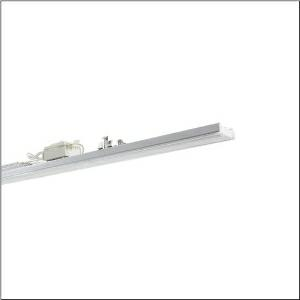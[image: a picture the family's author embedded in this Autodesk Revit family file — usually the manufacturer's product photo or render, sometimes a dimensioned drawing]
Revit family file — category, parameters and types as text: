
# Revit family: licross_r__11_recessed_mo_51tl10dn495g_bfc4
name_source: partatom
category: Lighting Fixtures
units: mm (PartAtom-declared; Revit-internal decimal feet)

## family parameters
Cut with Voids When Loaded = No
Host = Face
Light Source = No
Part Type = Normal
Room Calculation Point = No
Round Connector Dimension = Use Diameter
Shared = No

## types (1)
- --- (1 x LED, 9960 lm, 56.7 W, 4000K)
    Apparent Load = 57 VA
    CIE Flux Codes = 50 81 96 100 100
    Color Rendering = 80
    Color Temperature = 4000K
    Default Elevation = 1800 mm
    Description = Licross® 11 Recessed MO, luminaire insert, of sheet steel, coil coated, white, length: 1.500mm, width: 66mm, height: 67mm, LED rated luminous flux: 9.960lm, light colour: 840, control gear: DALI 2, with plug, 5-pole, with phase selection, mains connection: 220..240V, AC, 50/60Hz, rated input power: 57W, halogen-free wiring, primary optical cover: cover, of PMMA, light emission: direct distribution, primary light characteristic: symmetric, protection rating (complete): IP40, insulation class (complete): insulation class I (protective earthing), certification: CE, ENEC, VDE, UKCA, protection symbol: D if used in an environment without relevant dust loads with corresponding accessories, impact resistance: IK06, permissible ambient temperature for indoor applications: -25..+35°C, corresponds to IFS (International Featured Standards) requirements for safety and quality in the food industry, reducing of maximum allowable ambient temperature of 5°C with ceiling mounting, LABS conformity tested according to VDMA 24364:2018-05, packaging unit: 1 piece
    Height = 58 mm
    Lamp = 1 x LED
    Lamp Light Flux = 9960 lm
    Lamp Power = 56.7 W
    Lamp count = 1
    Length = 1500 mm
    Luminous efficacy = 176 lm/W
    Manufacturer = Siteco
    ModVariant = No
    Model = 51TL10DN495G
    Mounting Place = Ceiling
    Mounting Type = Pendant
    Number of Poles = 1
    OnlyDefault = Yes
    Power Factor = 1
    Product Name = Licross® 11 Recessed MO
    Product group = luminaire insert
    ProductGroupID = 902
    Protection Class = Protection class I
    Protection Degree = IP 40
    RLX_Detail_Level = 1
    RLX_Emergency_Light_Flux = 0 lm
    RLX_Emergency_Type = 0
    RLX_Emergency_Type_DB = No
    RlxData = <blob elided: 24277 chars, md5=c90bea5f>
    Socket = socket
    Standby Power = 0 W
    System Light Flux = 9960 lm
    System Power = 57 W
    Type Comments = factory setting: luminous flux: 100 % | dim-lin: 254 | 378 mA
    Type Image = l_1296930.jpg
    URL = http://relux.com
    VarID = @adj_099900
    Voltage = 0 V
    Weight = 0.00 kg
    Width = 66 mm

## geometry (parser evidence)
native form markers: Blend x4, Sweep x10
no freeform markers — native parametric forms only
